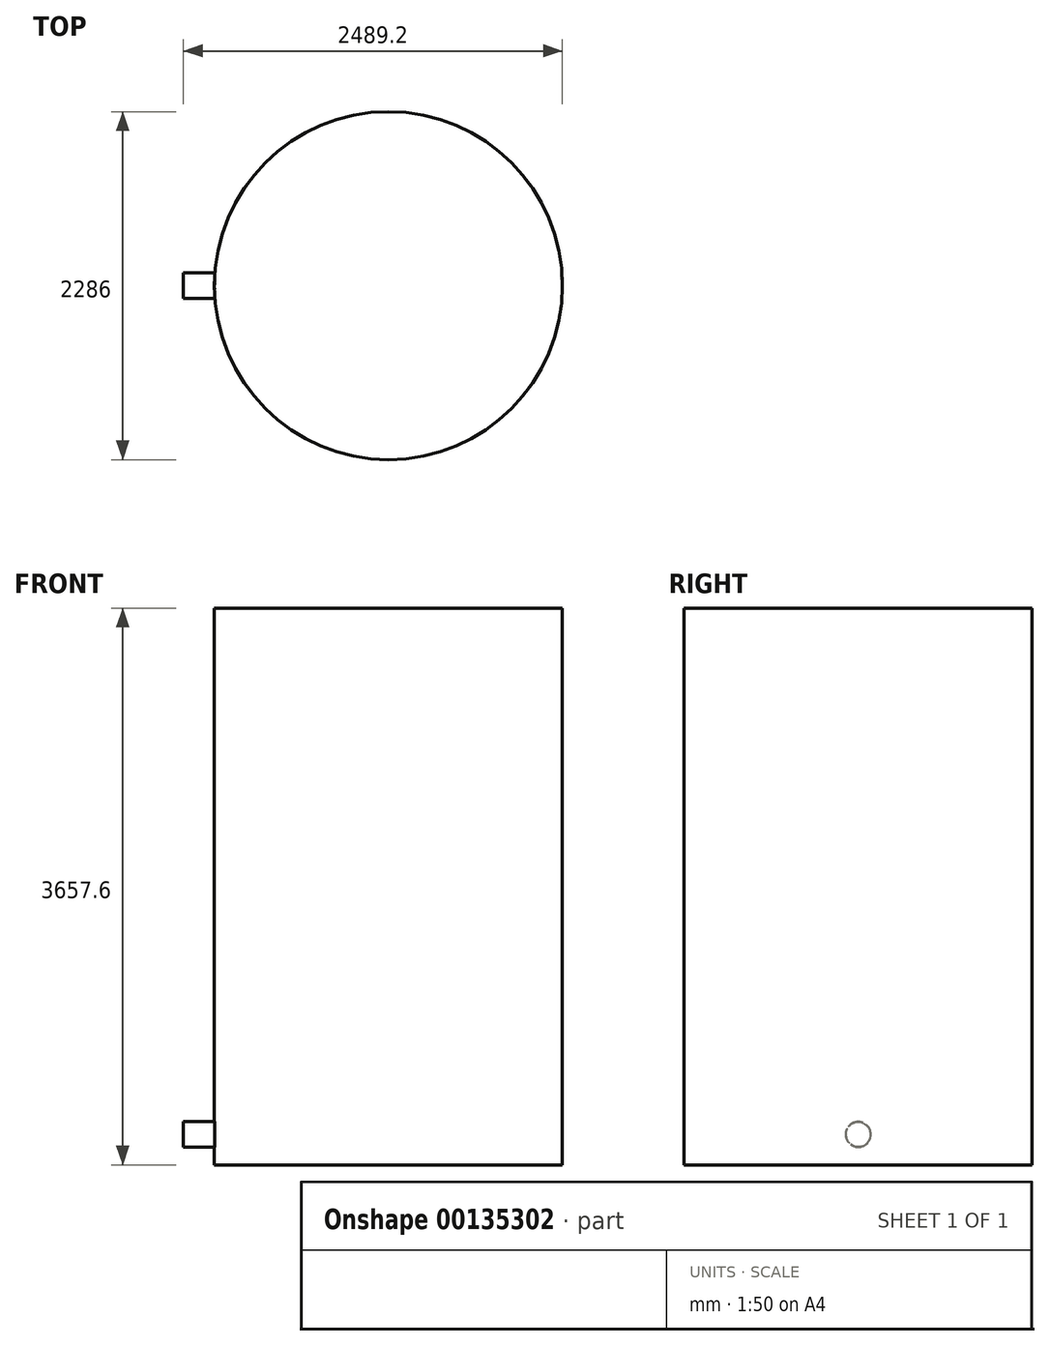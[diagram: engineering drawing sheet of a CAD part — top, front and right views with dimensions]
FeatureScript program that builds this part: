
annotation { "Feature Type Name" : "Feature", "Feature Type Description" : "" }
export const myFeature = defineFeature(function(context is Context, id is Id, definition is map)
    precondition{}
    {
        {
            var Q0;
            Q0=qCreatedBy(makeId("Top.planeOp"),FACE);
            var sketch = newSketch(context, id + "F0", { "sketchPlane" : qUnion([Q0])});
            skCircle(sketch, "E0", {"center": v(0, 0) * mm, "radius": 1143 * mm});
            skSolve(sketch);
        }
        {
            var Q0;
            Q0=makeQuery(id+"F0.imprint","IMPRINT",FACE,{"disambiguationData":[TD([[makeQuery(id+"F0.imprint","IMPRINT",EDGE,{"derivedFrom":sQuery(id+"F0.wireOp",EDGE,"E0")}),1.0]])]});
            extrude(context, id + "F1", {"entities" : qUnion([Q0]), "depth" : 3.17 * mm});
        }
        {
            var Q0;
            Q0=makeQuery(id+"F1.opExtrude","CAP_FACE",FACE,{"disambiguationData":[OSD([sQuery(id+"F0.wireOp",EDGE,"E0")])],"isStart":false});
            var sketch = newSketch(context, id + "F2", { "sketchPlane" : qUnion([Q0])});
            skCircle(sketch, "E1.0", {"center": v(0, 0) * mm, "radius": 1139.82 * mm});
            skSolve(sketch);
        }
        {
            var Q0;
            Q0=makeQuery(id+"F2.imprint","IMPRINT",FACE,{"disambiguationData":[TD([[makeQuery(id+"F2.imprint","IMPRINT",EDGE,{"derivedFrom":sQuery(id+"F2.wireOp",EDGE,"E1.0")}),-1.0]])]});
            extrude(context, id + "F3", {"entities" : qUnion([Q0]), "operationType" : NewBodyOperationType.ADD, "depth" : 3651.25 * mm});
        }
        {
            var Q0;
            Q0=makeQuery(id+"F3.opExtrude","CAP_FACE",FACE,{"disambiguationData":[OSD([sQuery(id+"F0.wireOp",EDGE,"E0"),sQuery(id+"F2.wireOp",EDGE,"E1.0")])],"isStart":false});
            var sketch = newSketch(context, id + "F4", { "sketchPlane" : qUnion([Q0])});
            skCircle(sketch, "E2.0", {"center": v(0, 0) * mm, "radius": 1143 * mm});
            skSolve(sketch);
        }
        {
            var Q0;
            Q0 = qSketchRegion(id + "F4", true);
            extrude(context, id + "F5", {"entities" : qUnion([Q0]), "operationType" : NewBodyOperationType.ADD, "depth" : 3.17 * mm});
        }
        {
            var Q0;
            Q0=makeQuery(id+"F5.opExtrude","CAP_FACE",FACE,{"disambiguationData":[OSD([sQuery(id+"F4.wireOp",EDGE,"E2.0")])],"isStart":false});
            var sketch = newSketch(context, id + "F6", { "sketchPlane" : qUnion([Q0])});
            skCircle(sketch, "E3.0", {"center": v(0, 0) * mm, "radius": 1143 * mm});
            skLineSegment(sketch, "E4", {"start": v(0, 0) * mm, "end": v(-1917.63, 0) * mm, "construction": true});
            skLineSegment(sketch, "E5", {"start": v(-1143, 615.75) * mm, "end": v(-1143, -813.3) * mm, "construction": true});
            skSolve(sketch);
        }
        {
            var Q0;
            Q0=sQuery(id+"F6.wireOp",EDGE,"E5");
            var Q1;
            {var subQ0=sQuery(id+"F0.wireOp",EDGE,"E0");Q1=makeQuery(id+"F5.boolean.opBoolean","MERGE",FACE,{"derivedFrom":[makeQuery(id+"F3.boolean.opBoolean","MERGE",FACE,{"derivedFrom":[makeQuery(id+"F1.opExtrude","SWEPT_FACE",FACE,{"disambiguationData":[OSD([subQ0])]}),makeQuery(id+"F3.opExtrude","SWEPT_FACE",FACE,{"disambiguationData":[OSD([subQ0])]})]}),makeQuery(id+"F5.opExtrude","SWEPT_FACE",FACE,{"disambiguationData":[OSD([sQuery(id+"F4.wireOp",EDGE,"E2.0")])]})]});}
            cPlane(context, id + "F7", {"entities" : qUnion([Q0, Q1]), "cplaneType" : CPlaneType.LINE_ANGLE, "offset" : 25.4 * mm, "angle" : 0 * degree, "width" : 152.4 * mm, "height" : 152.4 * mm});
        }
        {
            var Q0;
            Q0=qCreatedBy(id+"F7.planeOp",FACE);
            var sketch = newSketch(context, id + "F8", { "sketchPlane" : qUnion([Q0])});
            skLineSegment(sketch, "E6", {"start": v(0, 3415.83) * mm, "end": v(0, 0) * mm, "construction": true});
            skCircle(sketch, "E7", {"center": v(0, 200.03) * mm, "radius": 84.14 * mm});
            skCircle(sketch, "E8", {"center": v(0, 200.03) * mm, "radius": 80.6 * mm});
            skSolve(sketch);
        }
        {
            var Q0;
            Q0=makeQuery(id+"F8.imprint","IMPRINT",FACE,{"disambiguationData":[TD([[makeQuery(id+"F8.imprint","IMPRINT",EDGE,{"derivedFrom":sQuery(id+"F8.wireOp",EDGE,"E8")}),1.0]])]});
            var Q1;
            {var subQ0=sQuery(id+"F0.wireOp",EDGE,"E0");Q1=makeQuery(id+"F5.boolean.opBoolean","MERGE",FACE,{"derivedFrom":[makeQuery(id+"F3.boolean.opBoolean","MERGE",FACE,{"derivedFrom":[makeQuery(id+"F1.opExtrude","SWEPT_FACE",FACE,{"disambiguationData":[OSD([subQ0])]}),makeQuery(id+"F3.opExtrude","SWEPT_FACE",FACE,{"disambiguationData":[OSD([subQ0])]})]}),makeQuery(id+"F5.opExtrude","SWEPT_FACE",FACE,{"disambiguationData":[OSD([sQuery(id+"F4.wireOp",EDGE,"E2.0")])]})]});}
            var Q2;
            Q2=makeQuery(id+"F1.opExtrude","SWEPT_BODY",BODY,{"disambiguationData":[OSD([sQuery(id+"F0.wireOp",EDGE,"E0")])]});
            extrude(context, id + "F9", {"entities" : qUnion([Q0]), "operationType" : NewBodyOperationType.REMOVE, "endBoundEntityFace" : qUnion([Q1]), "endBoundEntityBody" : qUnion([Q2]), "depth" : 25.4 * mm});
        }
        {
            var Q0;
            Q0=makeQuery(id+"F8.imprint","IMPRINT",FACE,{"disambiguationData":[TD([[makeQuery(id+"F8.imprint","IMPRINT",EDGE,{"derivedFrom":sQuery(id+"F8.wireOp",EDGE,"E7")}),1.0]])]});
            extrude(context, id + "F10", {"entities" : qUnion([Q0]), "oppositeDirection" : true, "depth" : 203.2 * mm});
        }
        {
            var Q0;
            Q0=makeQuery(id+"F8.imprint","IMPRINT",FACE,{"disambiguationData":[TD([[makeQuery(id+"F8.imprint","IMPRINT",EDGE,{"derivedFrom":sQuery(id+"F8.wireOp",EDGE,"E7")}),1.0]])]});
            var Q1;
            Q1=makeQuery(id+"F1.opExtrude","SWEPT_BODY",BODY,{"disambiguationData":[OSD([sQuery(id+"F0.wireOp",EDGE,"E0")])]});
            extrude(context, id + "F11", {"entities" : qUnion([Q0]), "operationType" : NewBodyOperationType.ADD, "endBound" : BoundingType.UP_TO_NEXT, "endBoundEntityBody" : qUnion([Q1]), "depth" : 25.4 * mm, "hasSecondDirection" : true, "secondDirectionBound" : BoundingType.UP_TO_NEXT, "secondDirectionOppositeDirection" : true, "secondDirectionDepth" : 25.4 * mm});
        }
    });
